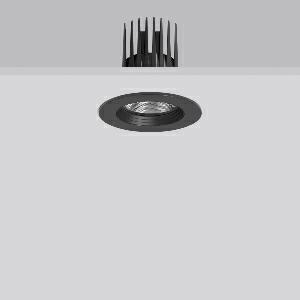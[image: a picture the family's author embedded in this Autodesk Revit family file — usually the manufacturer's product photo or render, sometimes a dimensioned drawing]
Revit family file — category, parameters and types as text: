
# Revit family: heledon_mini_e_901750_003_3_76_4261
name_source: partatom
category: Lighting Fixtures
units: mm (PartAtom-declared; Revit-internal decimal feet)

## family parameters
Cut with Voids When Loaded = No
Host = Face
Light Source = No
Part Type = Normal
Room Calculation Point = No
Round Connector Dimension = Use Diameter
Shared = No

## types (1)
- HELEDON mini E (1 x LED Modul 935, 3800 lm, 3500)
    Apparent Load = 29 VA
    Approval mark = CE
    CIE Flux Codes = 95 99 100 100 100
    Color Rendering = 92
    Color Temperature = 3500
    Default Elevation = 1800 mm
    Description = Series: HELEDON mini
Round recessed downlight. Housing: die-cast aluminium, powder-coated. Black plastic ring and recessed LED to prevent glare from the side. Optical assembly with reflector made of MIRO-Silver with 98% total light reflection for outstanding efficiency - can be changed without tools. Best colour rendering index Ra>90. Suitable for Recessed ceiling mounting. Installation without tools thanks to spring fastening system. Including separate LED converter with connecting cable 600 mm.High quality converter without flickering and stroboscopic effect. Through-wiring box (5 pole) available as accessory. The following accessories can be mounted without use of tools: interchangeable lenses, decorative glasses, honeycomb louvre, clear and frosted diffusers, white interchangeable plastic ring. 
Colour: deep black, matt (RAL 9005)
Diameter: 124 mm
Height: 3 mm
Cut-out diameter: 114 mm
Recess height: 170 mm
Luminaire: recess height: 120 mm
Lamp: LED
Socket: without socket
Colour temperature: 3500K
Colour rendering index (CRI): 92
System power: 29 W
Rated luminous flux: 3800 lm
Luminous efficiency: 131 lm/W
Control gear: Converter, dimmable, DALI
Protection class: II
Type of protection: IP 20
    Height = 0 mm  [stored 0 ft]
    Lamp = 1 x LED Modul 935
    Lamp Light Flux = 3800 lm
    Lamp count = 1
    Length = 124 mm
    Lifetime = 50000 h
    Luminous efficacy = 131 lm/W
    Manufacturer = RZB
    ModVariant = No
    Model = 901750.003.3.76
    Mounting Place = Ceiling
    Mounting Type = Recessed
    Number of Poles = 1
    OnlyDefault = Yes
    Power Factor = 1
    Product Name = HELEDON mini E
    Product group = Recessed downlights
    ProductGroupID = 402
    Protection Class = Protection class II
    Protection Degree = IP 20
    RLX_Detail_Level = 1
    RLX_Emergency_Light_Flux = 0 lm
    RLX_Emergency_Type = 0
    RLX_Emergency_Type_DB = No
    RlxData = <blob elided: 125473 chars, md5=e690a5ad>
    Socket = socket
    Standby Power = 0 W
    System Light Flux = 3800 lm
    System Power = 29 W
    Type Comments = Product without accessories
    Type Image = 901657.003.jpg
    URL = http://relux.com
    VarID = ---
    Voltage = 230 V
    Voltage Range = 220-240 V
    Weight = 0.00 kg
    Width = 0 mm  [stored 0 ft]

note: [stored X ft] marks values corroborated as IEEE doubles in the binary element streams (Revit-internal decimal feet)

## geometry (parser evidence)
native form markers: Blend x4, Sweep x9
no freeform markers — native parametric forms only
